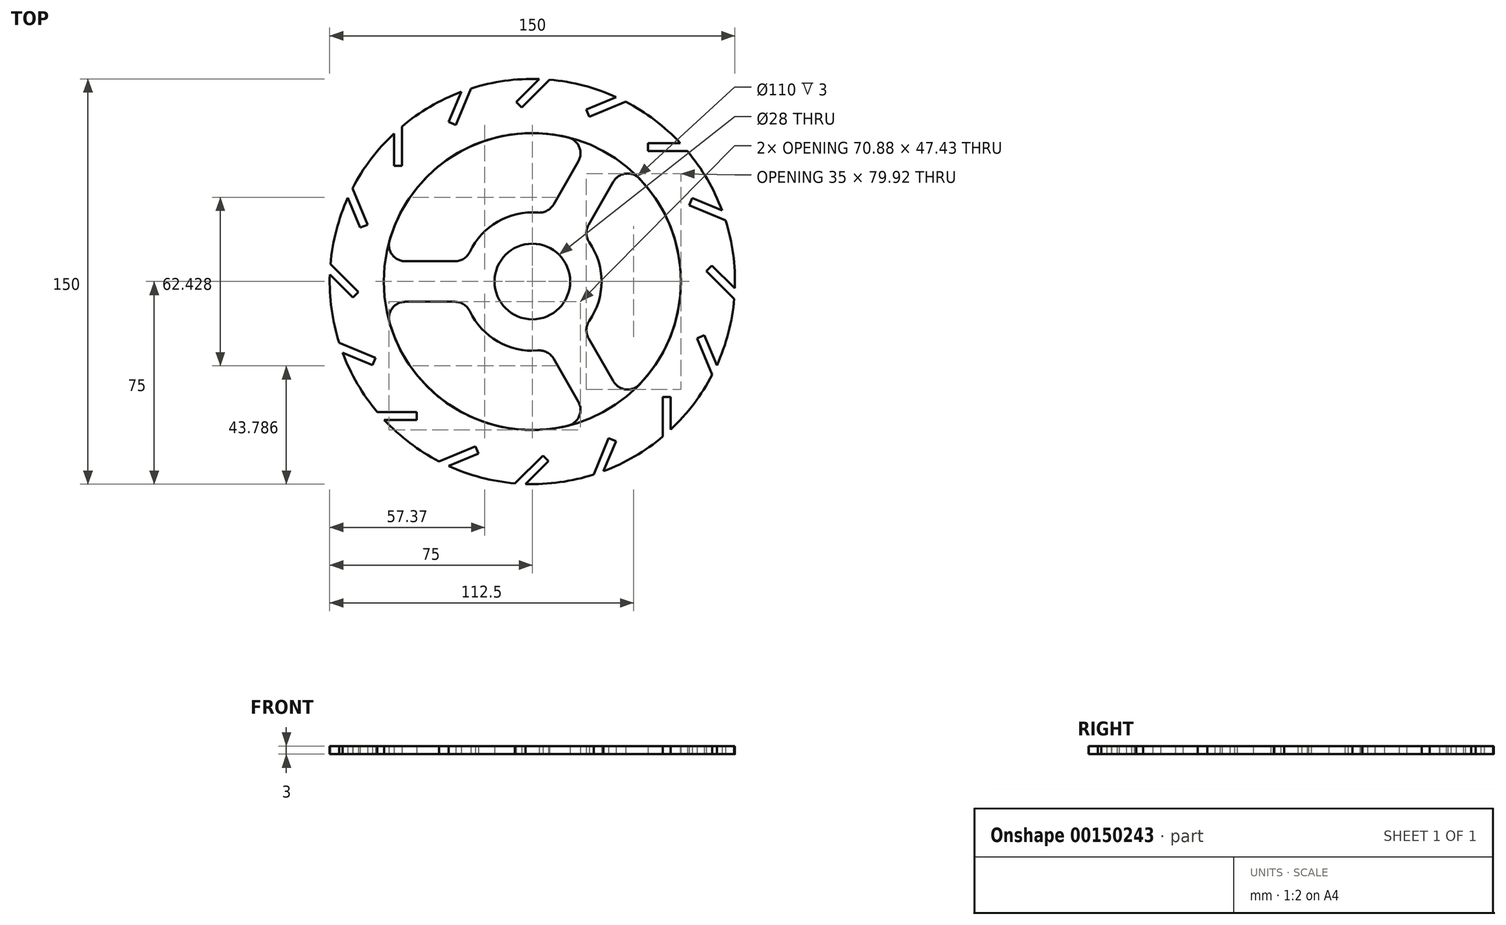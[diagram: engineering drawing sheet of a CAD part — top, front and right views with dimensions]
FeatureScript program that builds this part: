
annotation { "Feature Type Name" : "Feature", "Feature Type Description" : "" }
export const myFeature = defineFeature(function(context is Context, id is Id, definition is map)
    precondition{}
    {
        {
            assignVariable(context, id + "F0", {"name" : "WoodWidth", "anyValue" : 3});
        }
        {
            var Q0;
            Q0=qCreatedBy(makeId("Top.planeOp"),FACE);
            var sketch = newSketch(context, id + "F1", { "sketchPlane" : qUnion([Q0])});
            skCircle(sketch, "E0", {"center": v(0, 0) * mm, "radius": 75 * mm});
            skArc(sketch, "E1", {"start": v(13.21, 53.39) * mm, "mid": v(-27.5, 47.63) * mm, "end": v(-52.84, 15.25) * mm});
            skCircle(sketch, "E2", {"center": v(0, 0) * mm, "radius": 14 * mm});
            skLineSegment(sketch, "E3", {"start": v(-28.63, 7.5) * mm, "end": v(-47, 7.5) * mm});
            skLineSegment(sketch, "E4.MirrorCS", {"start": v(-28.63, -7.5) * mm, "end": v(-47, -7.5) * mm});
            skLineSegment(sketch, "E5.1.0", {"start": v(7.82, -28.54) * mm, "end": v(17, -44.46) * mm});
            skLineSegment(sketch, "E5.1.1", {"start": v(20.8, -21.04) * mm, "end": v(30, -36.96) * mm});
            skLineSegment(sketch, "E5.2.0", {"start": v(20.8, 21.04) * mm, "end": v(30, 36.96) * mm});
            skLineSegment(sketch, "E5.2.1", {"start": v(7.82, 28.54) * mm, "end": v(17, 44.46) * mm});
            skLineSegment(sketch, "E6", {"start": v(-51.2, 54.8) * mm, "end": v(-51.2, 42.8) * mm});
            skLineSegment(sketch, "E7", {"start": v(-51.2, 42.8) * mm, "end": v(-48.3, 42.8) * mm});
            skLineSegment(sketch, "E8", {"start": v(-48.3, 42.8) * mm, "end": v(-48.3, 57.37) * mm});
            skLineSegment(sketch, "E9.1.0", {"start": v(-63.69, 19.94) * mm, "end": v(-61, 21.05) * mm});
            skLineSegment(sketch, "E9.1.1", {"start": v(-68.28, 31.03) * mm, "end": v(-63.69, 19.94) * mm});
            skLineSegment(sketch, "E9.1.2", {"start": v(-61, 21.05) * mm, "end": v(-66.59, 34.51) * mm});
            skLineSegment(sketch, "E9.2.0", {"start": v(-66.47, -5.95) * mm, "end": v(-64.42, -3.9) * mm});
            skLineSegment(sketch, "E9.2.1", {"start": v(-74.96, 2.54) * mm, "end": v(-66.47, -5.95) * mm});
            skLineSegment(sketch, "E9.2.2", {"start": v(-64.42, -3.9) * mm, "end": v(-74.73, 6.4) * mm});
            skLineSegment(sketch, "E9.3.0", {"start": v(-59.14, -30.93) * mm, "end": v(-58.03, -28.26) * mm});
            skLineSegment(sketch, "E9.3.1", {"start": v(-70.22, -26.34) * mm, "end": v(-59.14, -30.93) * mm});
            skLineSegment(sketch, "E9.3.2", {"start": v(-58.03, -28.26) * mm, "end": v(-71.49, -22.68) * mm});
            skLineSegment(sketch, "E9.4.0", {"start": v(-42.8, -51.2) * mm, "end": v(-42.8, -48.3) * mm});
            skLineSegment(sketch, "E9.4.1", {"start": v(-54.8, -51.2) * mm, "end": v(-42.8, -51.2) * mm});
            skLineSegment(sketch, "E9.4.2", {"start": v(-42.8, -48.3) * mm, "end": v(-57.37, -48.3) * mm});
            skLineSegment(sketch, "E9.5.0", {"start": v(-19.94, -63.69) * mm, "end": v(-21.05, -61) * mm});
            skLineSegment(sketch, "E9.5.1", {"start": v(-31.03, -68.28) * mm, "end": v(-19.94, -63.69) * mm});
            skLineSegment(sketch, "E9.5.2", {"start": v(-21.05, -61) * mm, "end": v(-34.51, -66.59) * mm});
            skLineSegment(sketch, "E9.6.0", {"start": v(5.95, -66.47) * mm, "end": v(3.9, -64.42) * mm});
            skLineSegment(sketch, "E9.6.1", {"start": v(-2.54, -74.96) * mm, "end": v(5.95, -66.47) * mm});
            skLineSegment(sketch, "E9.6.2", {"start": v(3.9, -64.42) * mm, "end": v(-6.4, -74.73) * mm});
            skLineSegment(sketch, "E9.7.0", {"start": v(30.93, -59.14) * mm, "end": v(28.26, -58.03) * mm});
            skLineSegment(sketch, "E9.7.1", {"start": v(26.34, -70.22) * mm, "end": v(30.93, -59.14) * mm});
            skLineSegment(sketch, "E9.7.2", {"start": v(28.26, -58.03) * mm, "end": v(22.68, -71.49) * mm});
            skLineSegment(sketch, "E9.8.0", {"start": v(51.2, -42.8) * mm, "end": v(48.3, -42.8) * mm});
            skLineSegment(sketch, "E9.8.1", {"start": v(51.2, -54.8) * mm, "end": v(51.2, -42.8) * mm});
            skLineSegment(sketch, "E9.8.2", {"start": v(48.3, -42.8) * mm, "end": v(48.3, -57.37) * mm});
            skLineSegment(sketch, "E9.9.0", {"start": v(63.69, -19.94) * mm, "end": v(61, -21.05) * mm});
            skLineSegment(sketch, "E9.9.1", {"start": v(68.28, -31.03) * mm, "end": v(63.69, -19.94) * mm});
            skLineSegment(sketch, "E9.9.2", {"start": v(61, -21.05) * mm, "end": v(66.59, -34.51) * mm});
            skLineSegment(sketch, "E9.10.0", {"start": v(66.47, 5.95) * mm, "end": v(64.42, 3.9) * mm});
            skLineSegment(sketch, "E9.10.1", {"start": v(74.96, -2.54) * mm, "end": v(66.47, 5.95) * mm});
            skLineSegment(sketch, "E9.10.2", {"start": v(64.42, 3.9) * mm, "end": v(74.73, -6.4) * mm});
            skLineSegment(sketch, "E9.11.0", {"start": v(59.14, 30.93) * mm, "end": v(58.03, 28.26) * mm});
            skLineSegment(sketch, "E9.11.1", {"start": v(70.22, 26.34) * mm, "end": v(59.14, 30.93) * mm});
            skLineSegment(sketch, "E9.11.2", {"start": v(58.03, 28.26) * mm, "end": v(71.49, 22.68) * mm});
            skLineSegment(sketch, "E9.12.0", {"start": v(42.8, 51.2) * mm, "end": v(42.8, 48.3) * mm});
            skLineSegment(sketch, "E9.12.1", {"start": v(54.8, 51.2) * mm, "end": v(42.8, 51.2) * mm});
            skLineSegment(sketch, "E9.12.2", {"start": v(42.8, 48.3) * mm, "end": v(57.37, 48.3) * mm});
            skLineSegment(sketch, "E9.13.0", {"start": v(19.94, 63.69) * mm, "end": v(21.05, 61) * mm});
            skLineSegment(sketch, "E9.13.1", {"start": v(31.03, 68.28) * mm, "end": v(19.94, 63.69) * mm});
            skLineSegment(sketch, "E9.13.2", {"start": v(21.05, 61) * mm, "end": v(34.51, 66.59) * mm});
            skArc(sketch, "E10", {"start": v(2.07, 25.53) * mm, "mid": v(-12.8, 22.18) * mm, "end": v(-23.14, 10.97) * mm});
            skPoint(sketch, "E11.orphan", {"position": v(-0.58, 13.99) * mm});
            skPoint(sketch, "E12.orphan", {"position": v(12.4, 6.49) * mm});
            skPoint(sketch, "E13.orphan", {"position": v(-11.82, 7.5) * mm});
            skArc(sketch, "E14.trimOffspring", {"start": v(-23.14, -10.97) * mm, "mid": v(-12.8, -22.18) * mm, "end": v(2.07, -25.53) * mm});
            skPoint(sketch, "E15.orphan", {"position": v(-11.82, -7.5) * mm});
            skPoint(sketch, "E16.orphan", {"position": v(-0.58, -13.99) * mm});
            skPoint(sketch, "E17.orphan", {"position": v(12.4, -6.49) * mm});
            skArc(sketch, "E18.trimOffspring", {"start": v(21.07, -14.56) * mm, "mid": v(25.6, 0) * mm, "end": v(21.07, 14.56) * mm});
            skArc(sketch, "E19.trimOffspring", {"start": v(-52.84, -15.25) * mm, "mid": v(-27.5, -47.63) * mm, "end": v(13.21, -53.39) * mm});
            skArc(sketch, "E20.trimOffspring", {"start": v(39.63, -38.14) * mm, "mid": v(55, 0) * mm, "end": v(39.63, 38.14) * mm});
            skPoint(sketch, "E21.visualSharp", {"position": v(-24.49, 7.5) * mm});
            skArc(sketch, "E21.filletArc", {"start": v(-28.63, 7.5) * mm, "mid": v(-25.38, 8.44) * mm, "end": v(-23.14, 10.97) * mm});
            skPoint(sketch, "E22.visualSharp", {"position": v(-24.49, -7.5) * mm});
            skArc(sketch, "E22.filletArc", {"start": v(-23.14, -10.97) * mm, "mid": v(-25.38, -8.44) * mm, "end": v(-28.63, -7.5) * mm});
            skPoint(sketch, "E23.visualSharp", {"position": v(5.75, -24.96) * mm});
            skArc(sketch, "E23.filletArc", {"start": v(7.82, -28.54) * mm, "mid": v(5.38, -26.2) * mm, "end": v(2.07, -25.53) * mm});
            skPoint(sketch, "E24.visualSharp", {"position": v(18.74, -17.46) * mm});
            skArc(sketch, "E24.filletArc", {"start": v(21.07, -14.56) * mm, "mid": v(20, -17.76) * mm, "end": v(20.8, -21.04) * mm});
            skPoint(sketch, "E25.visualSharp", {"position": v(18.74, 17.46) * mm});
            skArc(sketch, "E25.filletArc", {"start": v(20.8, 21.04) * mm, "mid": v(20, 17.76) * mm, "end": v(21.07, 14.56) * mm});
            skPoint(sketch, "E26.visualSharp", {"position": v(5.75, 24.96) * mm});
            skArc(sketch, "E26.filletArc", {"start": v(2.07, 25.53) * mm, "mid": v(5.38, 26.2) * mm, "end": v(7.82, 28.54) * mm});
            skPoint(sketch, "E27.visualSharp", {"position": v(-54.49, 7.5) * mm});
            skArc(sketch, "E27.filletArc", {"start": v(-52.84, 15.25) * mm, "mid": v(-51.86, 9.92) * mm, "end": v(-47, 7.5) * mm});
            skPoint(sketch, "E28.visualSharp", {"position": v(-54.49, -7.5) * mm});
            skArc(sketch, "E28.filletArc", {"start": v(-47, -7.5) * mm, "mid": v(-51.86, -9.92) * mm, "end": v(-52.84, -15.25) * mm});
            skPoint(sketch, "E29.visualSharp", {"position": v(20.75, -50.94) * mm});
            skArc(sketch, "E29.filletArc", {"start": v(13.21, -53.39) * mm, "mid": v(17.34, -49.87) * mm, "end": v(17, -44.46) * mm});
            skPoint(sketch, "E30.visualSharp", {"position": v(33.74, -43.44) * mm});
            skArc(sketch, "E30.filletArc", {"start": v(30, -36.96) * mm, "mid": v(34.52, -39.95) * mm, "end": v(39.63, -38.14) * mm});
            skPoint(sketch, "E31.visualSharp", {"position": v(33.74, 43.44) * mm});
            skArc(sketch, "E31.filletArc", {"start": v(39.63, 38.14) * mm, "mid": v(34.52, 39.95) * mm, "end": v(30, 36.96) * mm});
            skPoint(sketch, "E32.visualSharp", {"position": v(20.75, 50.94) * mm});
            skArc(sketch, "E32.filletArc", {"start": v(17, 44.46) * mm, "mid": v(17.34, 49.87) * mm, "end": v(13.21, 53.39) * mm});
            skCircle(sketch, "E33", {"center": v(0, 0) * mm, "radius": 55 * mm});
            skLineSegment(sketch, "E34.1.14.0", {"start": v(-5.95, 66.47) * mm, "end": v(-3.9, 64.42) * mm});
            skLineSegment(sketch, "E34.3.14.0", {"start": v(2.54, 74.96) * mm, "end": v(-5.95, 66.47) * mm});
            skLineSegment(sketch, "E34.6.14.0", {"start": v(-3.9, 64.42) * mm, "end": v(6.4, 74.73) * mm});
            skLineSegment(sketch, "E34.1.15.0", {"start": v(-30.93, 59.14) * mm, "end": v(-28.26, 58.03) * mm});
            skLineSegment(sketch, "E34.3.15.0", {"start": v(-26.34, 70.22) * mm, "end": v(-30.93, 59.14) * mm});
            skLineSegment(sketch, "E34.6.15.0", {"start": v(-28.26, 58.03) * mm, "end": v(-22.68, 71.49) * mm});
            skSolve(sketch);
        }
        {
            var Q0;
            {var subQ22=sQuery(id+"F1.wireOp",EDGE,"E6");Q0=makeQuery(id+"F1.imprint","IMPRINT",FACE,{"disambiguationData":[TD([[makeQuery(id+"F1.imprint","IMPRINT",EDGE,{"derivedFrom":subQ22}),-1.0]])]});}
            var Q1;
            Q1=makeQuery(id+"F1.imprint","IMPRINT",FACE,{"disambiguationData":[TD([[makeQuery(id+"F1.imprint","IMPRINT",EDGE,{"derivedFrom":sQuery(id+"F1.wireOp",EDGE,"E2")}),-1.0]])]});
            extrude(context, id + "F2", {"entities" : qUnion([Q0, Q1]), "depth" : (getVariable(context, 'WoodWidth')) * mm});
        }
        {
            var Q0;
            {var subQ22=sQuery(id+"F1.wireOp",EDGE,"E6");Q0=makeQuery(id+"F1.imprint","IMPRINT",FACE,{"disambiguationData":[TD([[makeQuery(id+"F1.imprint","IMPRINT",EDGE,{"derivedFrom":subQ22}),-1.0]])]});}
            extrude(context, id + "F3", {"entities" : qUnion([Q0]), "depth" : 3 * mm});
        }
    });
